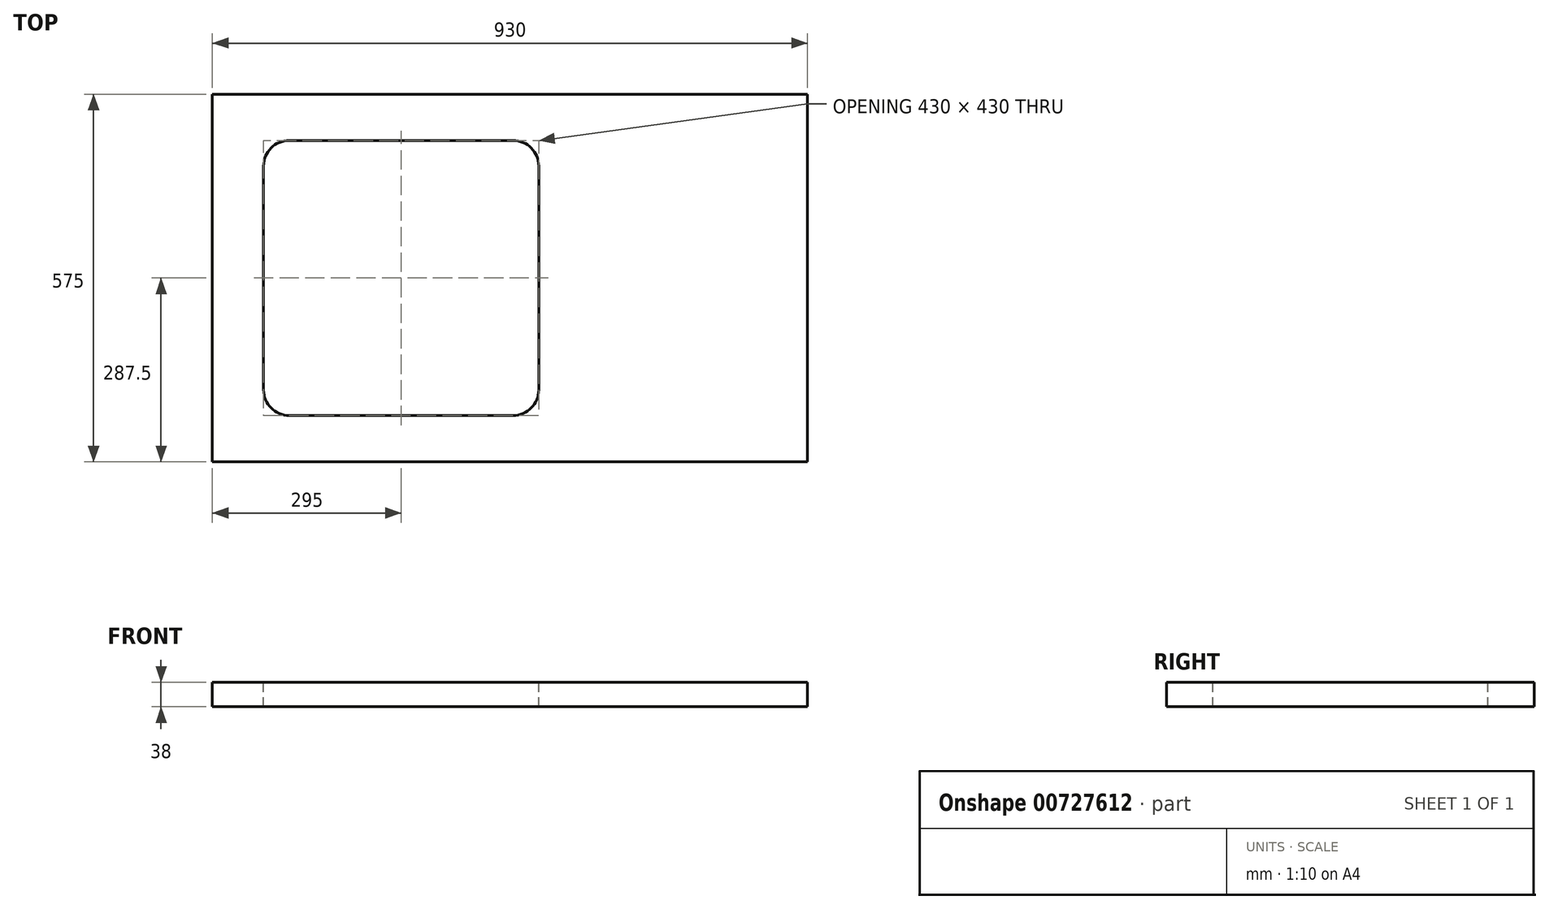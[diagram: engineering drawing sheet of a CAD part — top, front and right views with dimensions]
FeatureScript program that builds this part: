
annotation { "Feature Type Name" : "Feature", "Feature Type Description" : "" }
export const myFeature = defineFeature(function(context is Context, id is Id, definition is map)
    precondition{}
    {
        {
            var Q0;
            Q0=qCreatedBy(makeId("Top.planeOp"),FACE);
            var sketch = newSketch(context, id + "F0", { "sketchPlane" : qUnion([Q0])});
            skLineSegment(sketch, "E0.bottom", {"start": v(-465, 287.5) * mm, "end": v(465, 287.5) * mm});
            skLineSegment(sketch, "E0.top", {"start": v(-465, -287.5) * mm, "end": v(465, -287.5) * mm});
            skLineSegment(sketch, "E0.left", {"start": v(-465, 287.5) * mm, "end": v(-465, -287.5) * mm});
            skLineSegment(sketch, "E0.right", {"start": v(465, 287.5) * mm, "end": v(465, -287.5) * mm});
            skLineSegment(sketch, "E1", {"start": v(-465, 287.5) * mm, "end": v(465, -287.5) * mm, "construction": true});
            skSolve(sketch);
        }
        {
            var Q0;
            Q0 = qSketchRegion(id + "F0", true);
            extrude(context, id + "F1", {"entities" : qUnion([Q0]), "oppositeDirection" : true, "depth" : 38 * mm, "offsetDistance" : 25 * mm});
        }
        {
            var Q0;
            Q0=makeQuery(id+"F1.opExtrude","CAP_FACE",FACE,{"disambiguationData":[OSD([sQuery(id+"F0.wireOp",EDGE,"E0.bottom"),sQuery(id+"F0.wireOp",EDGE,"E0.top"),sQuery(id+"F0.wireOp",EDGE,"E0.left"),sQuery(id+"F0.wireOp",EDGE,"E0.right")])],"isStart":true});
            var sketch = newSketch(context, id + "F2", { "sketchPlane" : qUnion([Q0])});
            skLineSegment(sketch, "E2.bottom", {"start": v(-345, 215) * mm, "end": v(5, 215) * mm});
            skLineSegment(sketch, "E2.top", {"start": v(-345, -215) * mm, "end": v(5, -215) * mm});
            skLineSegment(sketch, "E2.left", {"start": v(-385, 175) * mm, "end": v(-385, -175) * mm});
            skLineSegment(sketch, "E2.right", {"start": v(45, 175) * mm, "end": v(45, -175) * mm});
            skPoint(sketch, "E3.visualSharp", {"position": v(-385, 215) * mm});
            skArc(sketch, "E3.filletArc", {"start": v(-345, 215) * mm, "mid": v(-373.28, 203.28) * mm, "end": v(-385, 175) * mm});
            skPoint(sketch, "E4.visualSharp", {"position": v(-385, -215) * mm});
            skArc(sketch, "E4.filletArc", {"start": v(-385, -175) * mm, "mid": v(-373.28, -203.28) * mm, "end": v(-345, -215) * mm});
            skPoint(sketch, "E5.visualSharp", {"position": v(45, -215) * mm});
            skArc(sketch, "E5.filletArc", {"start": v(5, -215) * mm, "mid": v(33.28, -203.28) * mm, "end": v(45, -175) * mm});
            skPoint(sketch, "E6.visualSharp", {"position": v(45, 215) * mm});
            skArc(sketch, "E6.filletArc", {"start": v(45, 175) * mm, "mid": v(33.28, 203.28) * mm, "end": v(5, 215) * mm});
            skLineSegment(sketch, "E7", {"start": v(-385, 0) * mm, "end": v(-465, 0) * mm, "construction": true});
            skSolve(sketch);
        }
        {
            var Q0;
            Q0 = qSketchRegion(id + "F2", true);
            extrude(context, id + "F3", {"entities" : qUnion([Q0]), "operationType" : NewBodyOperationType.REMOVE, "endBound" : BoundingType.THROUGH_ALL, "oppositeDirection" : true, "depth" : 25 * mm, "offsetDistance" : 25 * mm});
        }
    });
